# Revit family: P560260-031-30
name_source: partatom
category: Lighting Fixtures
revit_build: Autodesk Revit 2014 (Build: 20130308_1515(x64)
units: mm (PartAtom-declared; Revit-internal decimal feet)

## types (1)
- P560260-031-30
    Apparent Load = 10 VA
    Assembly Code = D5020200
    Color Filter = 16777215
    Connector Description = Lighting Connector
    Default Elevation = 48 "
    Description = Z-2025 LED Collection 1-Light Textured Black Frosted Glass LED Modern
Wall Light
    Dimming Lamp Color Temperature Shift = <None>
    Features = Frosted Glass Cylindrical
• Dimmable to 10% brightness (See Dimming Notes)
• Canopy covers a standard 4” recessed outlet box: 4.75 in W., 0.75 in ht., 4.75 in depth
• Mounting strap for outlet box included
• 6 in of wire supplied
• Americans With Disabilities Act (ADA) compliant
    Fixture distribution = Direct
    Glass = Paint - Hubbell - White Texture
    Housing Material = Paint - Hubbell - Textured Camera Black
    Lamp = LED
    Load Classification = Lighting
    Manufacturer = Progress Lighting
    Model = P560260-031-30
    Photometric Web File = generic
    Power Factor = 1
    Product Documentation Link = https://hubbellcdn.com
    Product Link = https://www.hubbell.com
    Tilt Angle = 60.00°
    URL = https://www.hubbell.com
    Voltage = 120 V
    Warranty = 1 year Warranty
    Wattage Comments = 9W
    Watts = 10 W

## geometry (parser evidence)
native form markers: Sweep x5
no freeform markers — native parametric forms only
